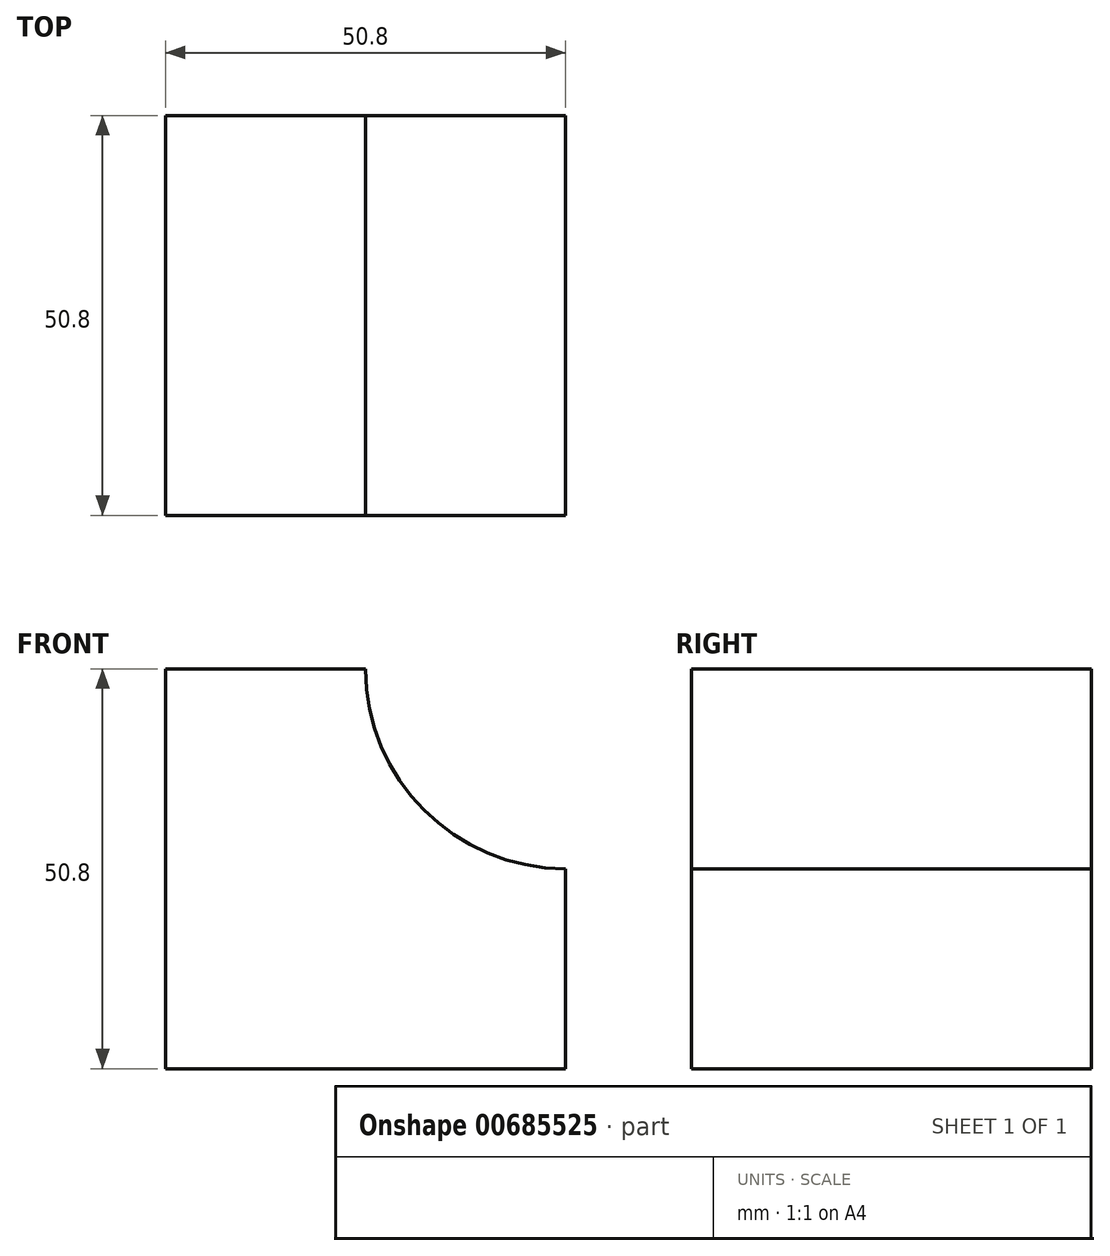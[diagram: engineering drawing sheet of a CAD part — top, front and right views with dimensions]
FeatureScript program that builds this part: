
annotation { "Feature Type Name" : "Feature", "Feature Type Description" : "" }
export const myFeature = defineFeature(function(context is Context, id is Id, definition is map)
    precondition{}
    {
        {
            var Q0;
            Q0=qCreatedBy(makeId("Front.planeOp"),FACE);
            var sketch = newSketch(context, id + "F0", { "sketchPlane" : qUnion([Q0])});
            skLineSegment(sketch, "E0", {"start": v(0, 0) * mm, "end": v(0, -50.8) * mm});
            skLineSegment(sketch, "E1", {"start": v(0, -50.8) * mm, "end": v(50.8, -50.8) * mm});
            skLineSegment(sketch, "E2", {"start": v(50.8, -50.8) * mm, "end": v(50.8, -25.4) * mm});
            skLineSegment(sketch, "E3", {"start": v(0, 0) * mm, "end": v(25.4, 0) * mm});
            skArc(sketch, "E4", {"start": v(25.4, 0) * mm, "mid": v(32.84, -17.96) * mm, "end": v(50.8, -25.4) * mm});
            skSolve(sketch);
        }
        {
            var Q0;
            Q0=makeQuery(id+"F0.imprint","IMPRINT",FACE,{"disambiguationData":[TD([[makeQuery(id+"F0.imprint","IMPRINT",EDGE,{"derivedFrom":sQuery(id+"F0.wireOp",EDGE,"E0")}),1.0]])]});
            extrude(context, id + "F1", {"entities" : qUnion([Q0]), "depth" : 50.8 * mm, "offsetDistance" : 25.4 * mm});
        }
    });
